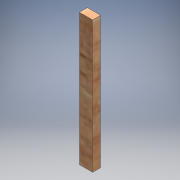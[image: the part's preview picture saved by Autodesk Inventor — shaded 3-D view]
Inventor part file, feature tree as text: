
AUTODESK INVENTOR PART (.ipt)
format: ipt  version: 2016 (Build 200138000, 138)  size: 97,792 bytes
history: native  units: mm
features: extrude x1, sketch x1
ambient origin geometry x8: Origin, YZ Plane, XZ Plane, XY Plane, X Axis, Y Axis, Z Axis, Center Point
bodies: Solid1 (feature_tree)
feature tree (2):
  extrude  "Extrusion1"  Depth=50.0mm
  sketch  "Sketch1"  dims[d0=5.0mm d1=50.0mm d2=3.0mm d3=0.0mm]
